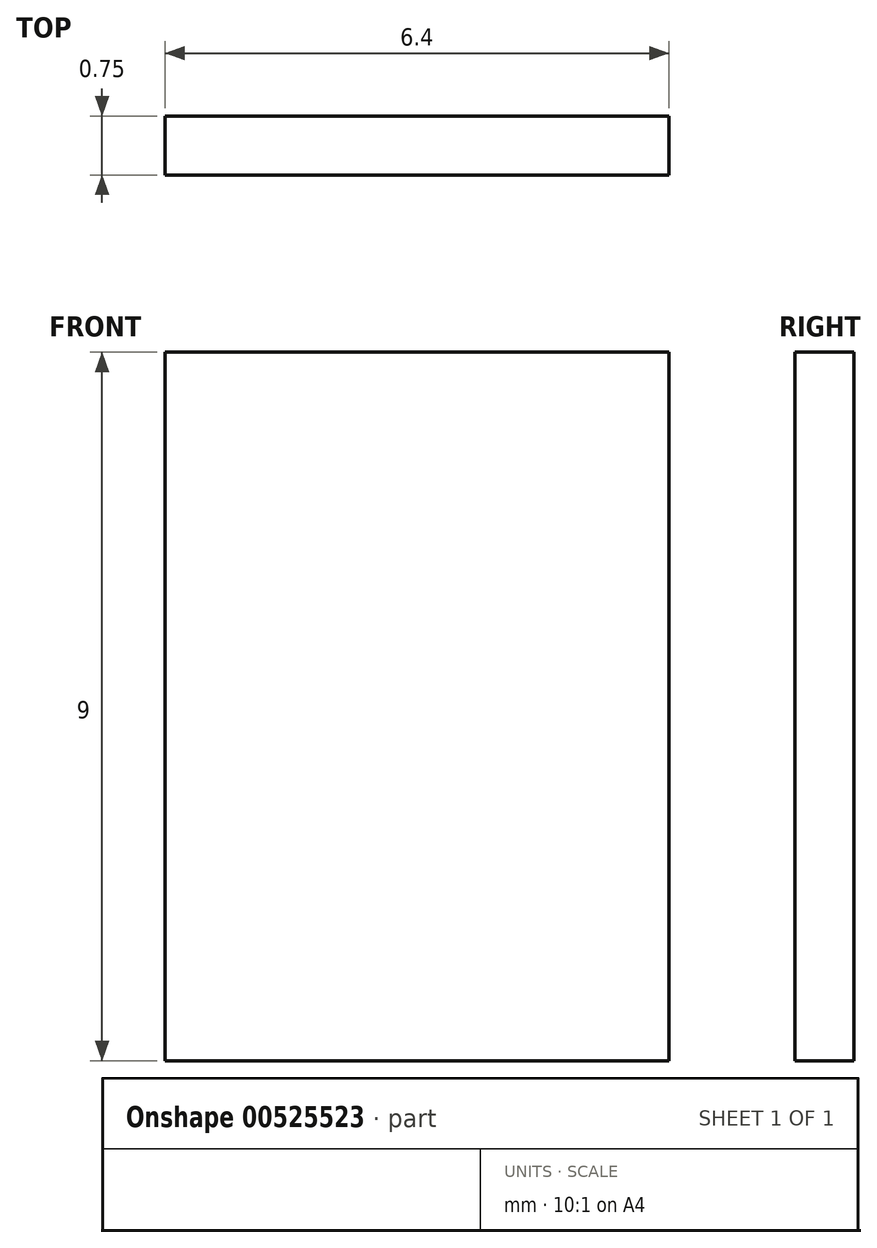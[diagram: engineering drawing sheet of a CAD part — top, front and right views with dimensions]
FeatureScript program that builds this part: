
annotation { "Feature Type Name" : "Feature", "Feature Type Description" : "" }
export const myFeature = defineFeature(function(context is Context, id is Id, definition is map)
    precondition{}
    {
        {
            var Q0;
            Q0=qCreatedBy(makeId("Front.planeOp"),FACE);
            var sketch = newSketch(context, id + "F0", { "sketchPlane" : qUnion([Q0])});
            skLineSegment(sketch, "E0.bottom", {"start": v(0, 0) * mm, "end": v(6.4, 0) * mm});
            skLineSegment(sketch, "E0.top", {"start": v(0, -9) * mm, "end": v(6.4, -9) * mm});
            skLineSegment(sketch, "E0.left", {"start": v(0, 0) * mm, "end": v(0, -9) * mm});
            skLineSegment(sketch, "E0.right", {"start": v(6.4, 0) * mm, "end": v(6.4, -9) * mm});
            skSolve(sketch);
        }
        {
            var Q0;
            Q0=makeQuery(id+"F0.imprint","IMPRINT",FACE,{"disambiguationData":[TD([[makeQuery(id+"F0.imprint","IMPRINT",EDGE,{"derivedFrom":sQuery(id+"F0.wireOp",EDGE,"E0.bottom")}),-1.0]])]});
            extrude(context, id + "F1", {"entities" : qUnion([Q0]), "depth" : .75 * mm, "offsetDistance" : 25.4 * mm});
        }
    });
